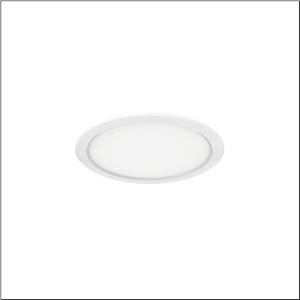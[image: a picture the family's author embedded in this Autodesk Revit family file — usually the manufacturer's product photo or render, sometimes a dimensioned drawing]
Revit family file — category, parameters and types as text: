
# Revit family: lunis_41_eco_51ds107f34a
name_source: partatom
category: Lighting Fixtures
units: mm (PartAtom-declared; Revit-internal decimal feet)

## family parameters
Cut with Voids When Loaded = No
Host = Face
Light Source = No
Part Type = Normal
Room Calculation Point = No
Round Connector Dimension = Use Diameter
Shared = No

## types (1)
- Lunis 41 ECO (1 x LED, 2200 lm, 22 W, 3000K)
    Apparent Load = 22 VA
    CIE Flux Codes = 47 80 97 100 100
    Color Rendering = 80
    Color Temperature = 3000K
    Default Elevation = 1800 mm
    Description = Lunis 41,  ECO, downlight, light emission: direct distribution, LED rated luminous flux: 2.200lm, light colour: 830, control gear: ECG, mains connection: 230V, AC, 50/60Hz, housing, round, of aluminium, coated, traffic white (RAL 9016), diameter: 216mm, recess depth: 58mm, protection rating (complete): IP20, protection rating (on room side): IP40, insulation class (complete): insulation class II (safety insulation), certification: CE, permissible ambient temperature for indoor applications: -20..+40°C, packaging unit: 1 piece
    Height = 0 mm  [stored 0 ft]
    Lamp = 1 x LED
    Lamp Light Flux = 2200 lm
    Lamp Power = 22 W
    Lamp count = 1
    Length = 216 mm
    Luminous efficacy = 100 lm/W
    Manufacturer = Siteco
    ModVariant = No
    Model = 51DS107F34A
    Mounting Place = Ceiling
    Mounting Type = Recessed
    Number of Poles = 1
    OnlyDefault = Yes
    Power Factor = 1
    Product Name = Lunis 41 ECO
    Product group = downlight
    ProductGroupID = 400
    Protection Class = Protection class II
    Protection Degree = IP 20
    RLX_Detail_Level = 1
    RLX_Emergency_Light_Flux = 0 lm
    RLX_Emergency_Type = 0
    RLX_Emergency_Type_DB = No
    RlxData = <blob elided: 22765 chars, md5=ef0c7b00>
    Socket = socket
    Standby Power = 0 W
    System Light Flux = 2200 lm
    System Power = 22 W
    Type Comments = Product without accessories
    Type Image = l_1007043.jpg
    URL = http://relux.com
    VarID = ---
    Voltage = 0 V
    Weight = 0.00 kg
    Width = 0 mm  [stored 0 ft]

note: [stored X ft] marks values corroborated as IEEE doubles in the binary element streams (Revit-internal decimal feet)

## geometry (parser evidence)
native form markers: Blend x4, Sweep x10
no freeform markers — native parametric forms only
